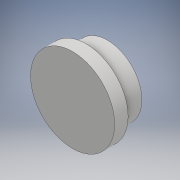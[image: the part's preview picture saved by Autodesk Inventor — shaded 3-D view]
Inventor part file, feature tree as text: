
AUTODESK INVENTOR PART (.ipt)
format: ipt  version: 2018 (Build 220112000, 112)  size: 110,592 bytes
history: native  units: mm
features: extrude x3, sketch x3
ambient origin geometry x8: Origin, YZ Plane, XZ Plane, XY Plane, X Axis, Y Axis, Z Axis, Center Point
bodies: Solid1 (feature_tree)
feature tree (6):
  extrude  "Extrusion1"  Depth=4.0mm TaperAngle=0.0deg
  extrude  "Extrusion2"  Depth=6.35mm TaperAngle=0.0deg
  extrude  "Extrusion3"  Depth=2.5mm TaperAngle=0.0deg
  sketch  "Sketch1"  dims[d0=25.0mm d1=4.0mm d2=0.0mm]
  sketch  "Sketch2"  dims[d3=20.5mm d4=6.35mm d5=0.0mm]
  sketch  "Sketch3"  dims[d6=8.0mm d7=2.5mm d8=0.0mm]
